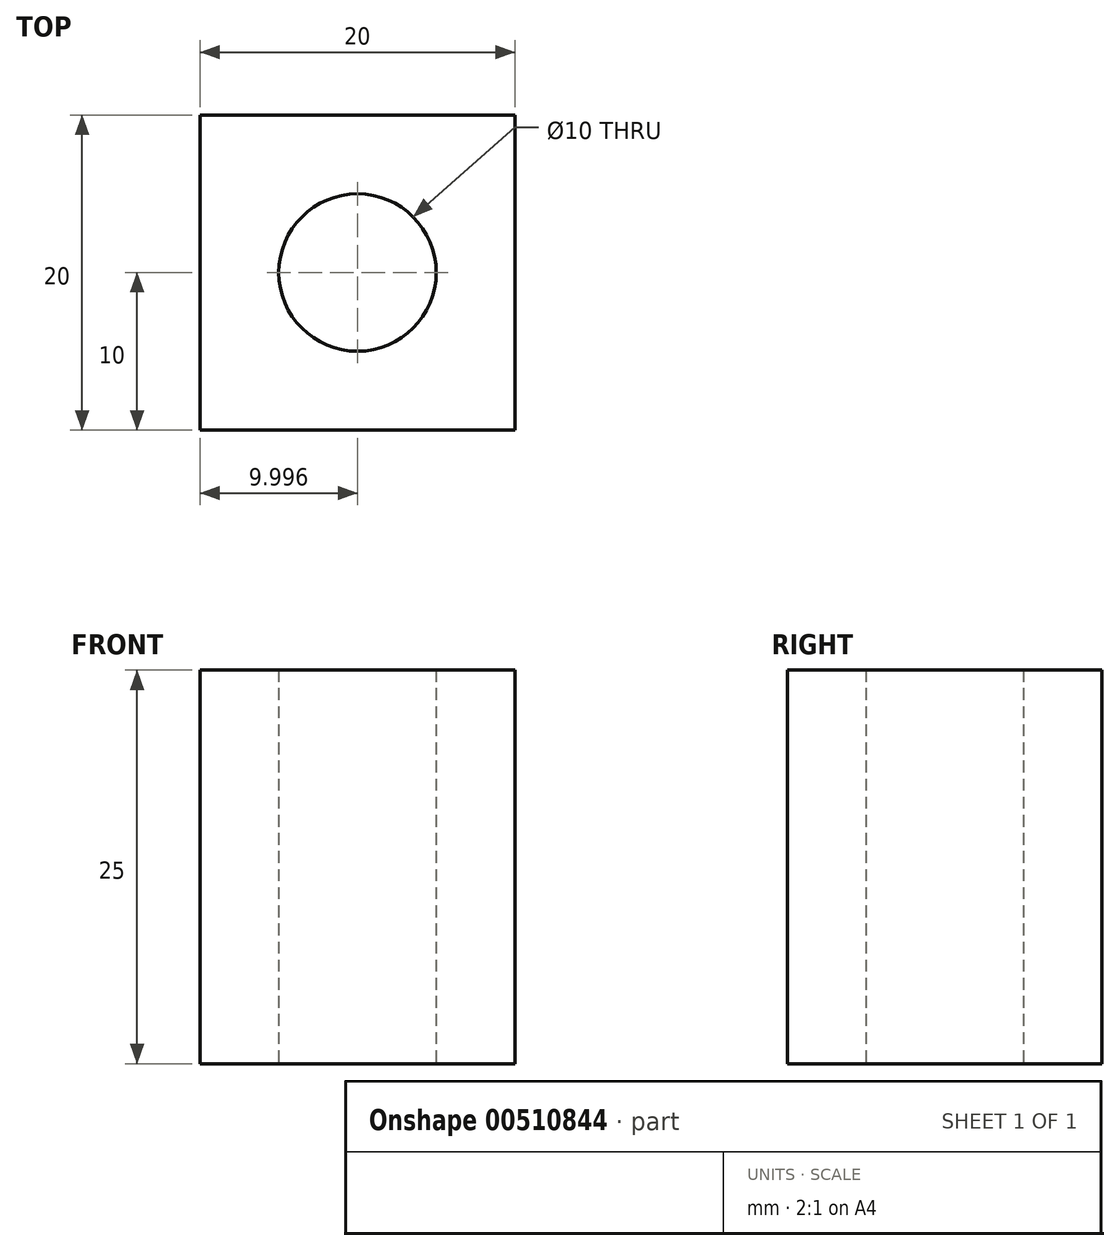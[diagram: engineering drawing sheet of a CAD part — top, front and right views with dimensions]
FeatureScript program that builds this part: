
annotation { "Feature Type Name" : "Feature", "Feature Type Description" : "" }
export const myFeature = defineFeature(function(context is Context, id is Id, definition is map)
    precondition{}
    {
        {
            var Q0;
            Q0=qCreatedBy(makeId("Top.planeOp"),FACE);
            var sketch = newSketch(context, id + "F0", { "sketchPlane" : qUnion([Q0])});
            skLineSegment(sketch, "E0", {"start": v(-48.7, -19.78) * mm, "end": v(-28.7, -19.78) * mm});
            skLineSegment(sketch, "E1", {"start": v(-28.7, -19.78) * mm, "end": v(-28.7, -39.78) * mm});
            skLineSegment(sketch, "E2", {"start": v(-28.7, -39.78) * mm, "end": v(-48.7, -39.78) * mm});
            skLineSegment(sketch, "E3", {"start": v(-48.7, -39.78) * mm, "end": v(-48.7, -19.78) * mm});
            skCircle(sketch, "E4", {"center": v(-38.7, -29.78) * mm, "radius": 5 * mm});
            skPoint(sketch, "E4.centerSnap0", {"position": v(-48.7, -29.78) * mm});
            skPoint(sketch, "E4.centerSnap1", {"position": v(-38.7, -19.78) * mm});
            skSolve(sketch);
        }
        {
            var Q0;
            Q0 = qSketchRegion(id + "F0", true);
            extrude(context, id + "F1", {"entities" : qUnion([Q0]), "depth" : 25 * mm});
        }
    });
